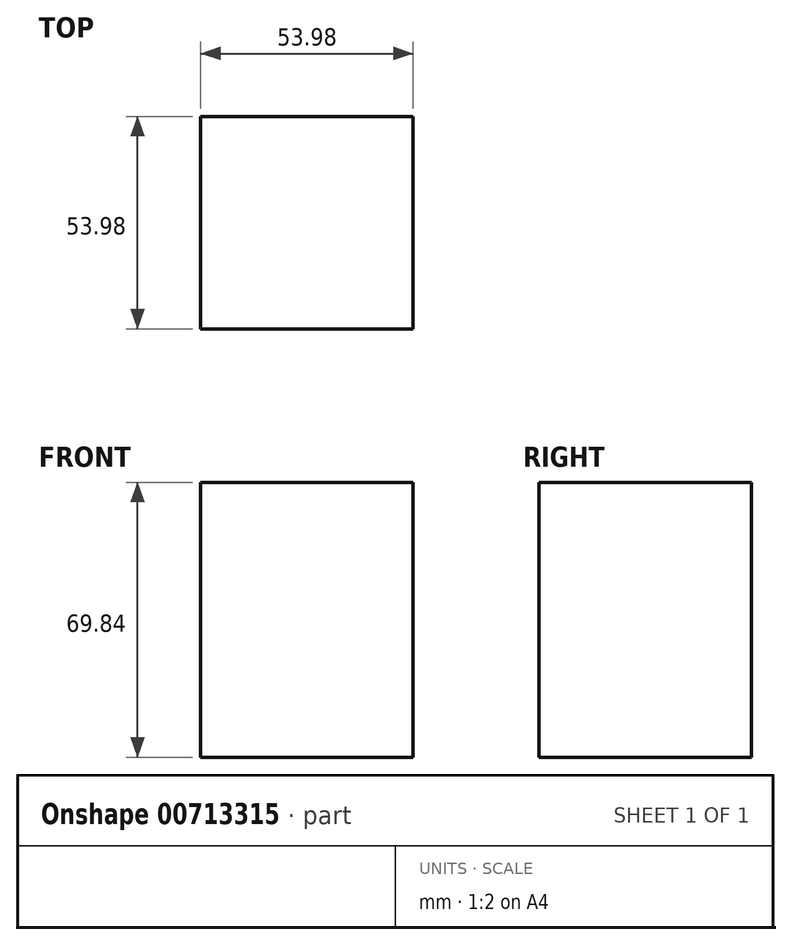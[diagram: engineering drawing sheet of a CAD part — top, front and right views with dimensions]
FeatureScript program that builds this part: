
annotation { "Feature Type Name" : "Feature", "Feature Type Description" : "" }
export const myFeature = defineFeature(function(context is Context, id is Id, definition is map)
    precondition{}
    {
        {
            var Q0;
            Q0=qCreatedBy(makeId("Top.planeOp"),FACE);
            var sketch = newSketch(context, id + "F0", { "sketchPlane" : qUnion([Q0])});
            skLineSegment(sketch, "E0.bottom", {"start": v(26.99, -26.99) * mm, "end": v(-26.99, -26.99) * mm});
            skLineSegment(sketch, "E0.top", {"start": v(26.99, 26.99) * mm, "end": v(-26.99, 26.99) * mm});
            skLineSegment(sketch, "E0.left", {"start": v(26.99, -26.99) * mm, "end": v(26.99, 26.99) * mm});
            skLineSegment(sketch, "E0.right", {"start": v(-26.99, -26.99) * mm, "end": v(-26.99, 26.99) * mm});
            skPoint(sketch, "E0.middle", {"position": v(0, 0) * mm});
            skSolve(sketch);
        }
        {
            var Q0;
            Q0 = qSketchRegion(id + "F0", true);
            extrude(context, id + "F1", {"entities" : qUnion([Q0]), "endBound" : BoundingType.SYMMETRIC, "depth" : 69.85 * mm, "offsetDistance" : 25.4 * mm});
        }
    });
